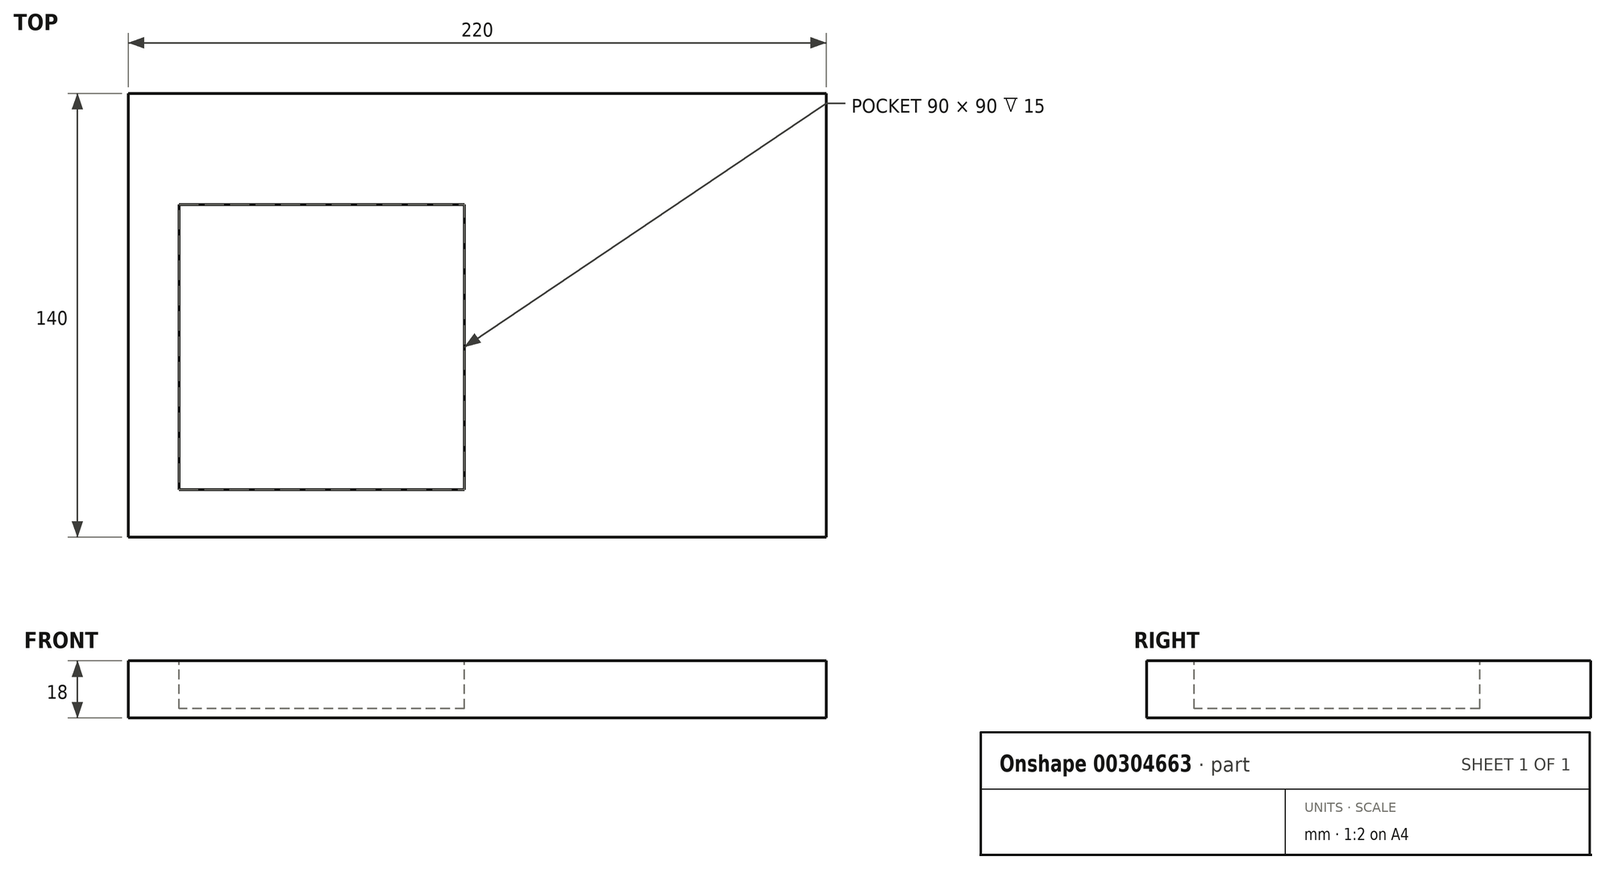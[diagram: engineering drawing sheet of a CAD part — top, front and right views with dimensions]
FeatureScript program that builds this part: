
annotation { "Feature Type Name" : "Feature", "Feature Type Description" : "" }
export const myFeature = defineFeature(function(context is Context, id is Id, definition is map)
    precondition{}
    {
        {
            var Q0;
            Q0=qCreatedBy(makeId("Top.planeOp"),FACE);
            var sketch = newSketch(context, id + "F0", { "sketchPlane" : qUnion([Q0])});
            skPoint(sketch, "E0.middle", {"position": v(0, 0) * mm});
            skLineSegment(sketch, "E1.bottom", {"start": v(110, -70) * mm, "end": v(-110, -70) * mm});
            skLineSegment(sketch, "E1.top", {"start": v(110, 70) * mm, "end": v(-110, 70) * mm});
            skLineSegment(sketch, "E1.left", {"start": v(110, -70) * mm, "end": v(110, 70) * mm});
            skLineSegment(sketch, "E1.right", {"start": v(-110, -70) * mm, "end": v(-110, 70) * mm});
            skSolve(sketch);
        }
        {
            var Q0;
            Q0=makeQuery(id+"F0.imprint","IMPRINT",FACE,{"disambiguationData":[TD([[makeQuery(id+"F0.imprint","IMPRINT",EDGE,{"derivedFrom":sQuery(id+"F0.wireOp",EDGE,"E1.bottom")}),-1.0]])]});
            extrude(context, id + "F1", {"entities" : qUnion([Q0]), "depth" : 18 * mm});
        }
        {
            var Q0;
            Q0=makeQuery(id+"F1.opExtrude","CAP_FACE",FACE,{"disambiguationData":[OSD([sQuery(id+"F0.wireOp",EDGE,"E1.bottom"),sQuery(id+"F0.wireOp",EDGE,"E1.top"),sQuery(id+"F0.wireOp",EDGE,"E1.left"),sQuery(id+"F0.wireOp",EDGE,"E1.right")])],"isStart":false});
            var sketch = newSketch(context, id + "F2", { "sketchPlane" : qUnion([Q0])});
            skLineSegment(sketch, "E2", {"start": v(0, 70) * mm, "end": v(0, -70) * mm});
            skLineSegment(sketch, "E3.bottom", {"start": v(-4, 35) * mm, "end": v(-94, 35) * mm});
            skLineSegment(sketch, "E3.top", {"start": v(-4, -55) * mm, "end": v(-94, -55) * mm});
            skLineSegment(sketch, "E3.left", {"start": v(-4, 35) * mm, "end": v(-4, -55) * mm});
            skLineSegment(sketch, "E3.right", {"start": v(-94, 35) * mm, "end": v(-94, -55) * mm});
            skSolve(sketch);
        }
        {
            var Q0;
            Q0=qSketchRegion(id+"F2",true);
            extrude(context, id + "F3", {"entities" : qUnion([Q0]), "operationType" : NewBodyOperationType.REMOVE, "oppositeDirection" : true, "depth" : 15 * mm});
        }
    });
